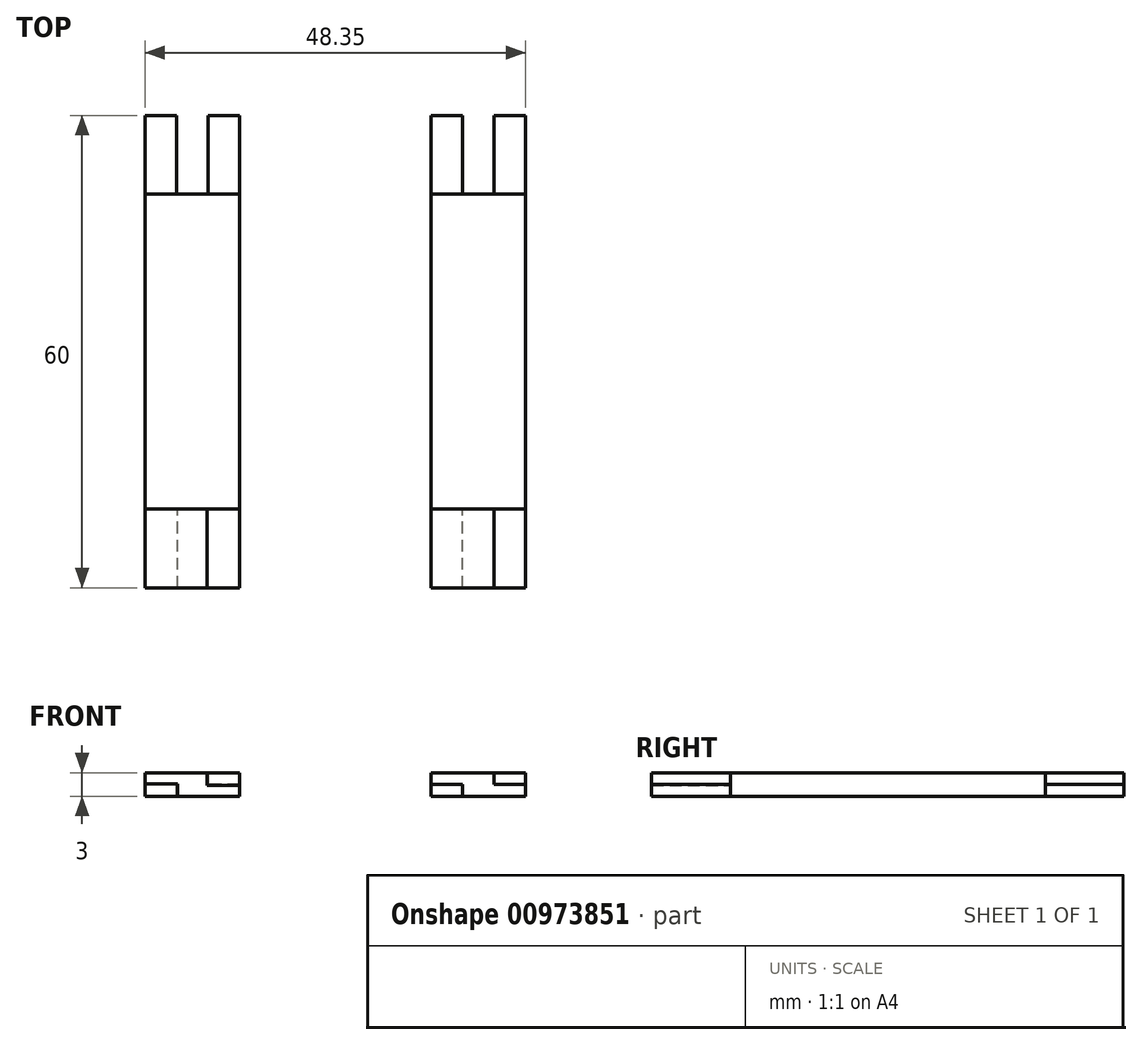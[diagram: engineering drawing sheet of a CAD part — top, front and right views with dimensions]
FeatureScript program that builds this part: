
annotation { "Feature Type Name" : "Feature", "Feature Type Description" : "" }
export const myFeature = defineFeature(function(context is Context, id is Id, definition is map)
    precondition{}
    {
        {
            var Q0;
            Q0=qCreatedBy(makeId("Top.planeOp"),FACE);
            var sketch = newSketch(context, id + "F0", { "sketchPlane" : qUnion([Q0])});
            skLineSegment(sketch, "E0.bottom", {"start": v(-16.75, 40) * mm, "end": v(-28.75, 40) * mm});
            skLineSegment(sketch, "E0.top", {"start": v(-16.75, 0) * mm, "end": v(-28.75, 0) * mm});
            skLineSegment(sketch, "E0.left", {"start": v(-16.75, 40) * mm, "end": v(-16.75, 0) * mm});
            skLineSegment(sketch, "E0.right", {"start": v(-28.75, 40) * mm, "end": v(-28.75, 0) * mm});
            skLineSegment(sketch, "E1.bottom", {"start": v(19.6, 40) * mm, "end": v(7.6, 40) * mm});
            skLineSegment(sketch, "E1.top", {"start": v(19.6, 0) * mm, "end": v(7.6, 0) * mm});
            skLineSegment(sketch, "E1.left", {"start": v(19.6, 40) * mm, "end": v(19.6, 0) * mm});
            skLineSegment(sketch, "E1.right", {"start": v(7.6, 40) * mm, "end": v(7.6, 0) * mm});
            skSolve(sketch);
        }
        {
            var Q0;
            Q0=makeQuery(id+"F0.imprint","IMPRINT",FACE,{"disambiguationData":[TD([[makeQuery(id+"F0.imprint","IMPRINT",EDGE,{"derivedFrom":sQuery(id+"F0.wireOp",EDGE,"E0.bottom")}),1.0]])]});
            var Q1;
            Q1=makeQuery(id+"F0.imprint","IMPRINT",FACE,{"disambiguationData":[TD([[makeQuery(id+"F0.imprint","IMPRINT",EDGE,{"derivedFrom":sQuery(id+"F0.wireOp",EDGE,"E1.bottom")}),1.0]])]});
            extrude(context, id + "F1", {"entities" : qUnion([Q0, Q1]), "depth" : 3 * mm, "offsetDistance" : 25 * mm});
        }
        {
            var Q0;
            Q0=makeQuery(id+"F1.opExtrude","SWEPT_FACE",FACE,{"disambiguationData":[OSD([sQuery(id+"F0.wireOp",EDGE,"E0.top")])]});
            var sketch = newSketch(context, id + "F2", { "sketchPlane" : qUnion([Q0])});
            skLineSegment(sketch, "E2", {"start": v(-28.75, 3) * mm, "end": v(-20.85, 3) * mm});
            skLineSegment(sketch, "E3", {"start": v(-20.85, 3) * mm, "end": v(-20.85, 1.4) * mm});
            skLineSegment(sketch, "E4", {"start": v(-20.85, 1.4) * mm, "end": v(-16.75, 1.4) * mm});
            skLineSegment(sketch, "E5", {"start": v(-16.75, 1.4) * mm, "end": v(-16.75, 0) * mm});
            skLineSegment(sketch, "E6", {"start": v(-16.75, 0) * mm, "end": v(-24.65, 0) * mm});
            skLineSegment(sketch, "E7", {"start": v(-24.65, 0) * mm, "end": v(-24.65, 1.6) * mm});
            skLineSegment(sketch, "E8", {"start": v(-24.65, 1.6) * mm, "end": v(-28.75, 1.6) * mm});
            skLineSegment(sketch, "E9", {"start": v(-28.75, 1.6) * mm, "end": v(-28.75, 3) * mm});
            skSolve(sketch);
        }
        {
            var Q0;
            Q0=makeQuery(id+"F1.opExtrude","SWEPT_FACE",FACE,{"disambiguationData":[OSD([sQuery(id+"F0.wireOp",EDGE,"E1.top")])]});
            var sketch = newSketch(context, id + "F3", { "sketchPlane" : qUnion([Q0])});
            skLineSegment(sketch, "E10", {"start": v(7.6, 3) * mm, "end": v(15.6, 3) * mm});
            skLineSegment(sketch, "E11", {"start": v(15.6, 3) * mm, "end": v(15.6, 1.5) * mm});
            skLineSegment(sketch, "E12", {"start": v(15.6, 1.5) * mm, "end": v(19.6, 1.5) * mm});
            skLineSegment(sketch, "E13", {"start": v(19.6, 1.5) * mm, "end": v(19.6, 0) * mm});
            skLineSegment(sketch, "E14", {"start": v(19.6, 0) * mm, "end": v(11.6, 0) * mm});
            skLineSegment(sketch, "E15", {"start": v(11.6, 0) * mm, "end": v(11.6, 1.5) * mm});
            skLineSegment(sketch, "E16", {"start": v(11.6, 1.5) * mm, "end": v(7.6, 1.5) * mm});
            skLineSegment(sketch, "E17", {"start": v(7.6, 1.5) * mm, "end": v(7.6, 3) * mm});
            skSolve(sketch);
        }
        {
            var Q0;
            Q0=makeQuery(id+"F2.imprint","IMPRINT",FACE,{"disambiguationData":[TD([[makeQuery(id+"F2.imprint","IMPRINT",EDGE,{"derivedFrom":sQuery(id+"F2.wireOp",EDGE,"5EJuN7WN-PZEX-N2uI-UbYe-ZOfutWstvHtY")}),1.0]])]});
            var Q1;
            Q1=makeQuery(id+"F3.imprint","IMPRINT",FACE,{"disambiguationData":[TD([[makeQuery(id+"F3.imprint","IMPRINT",EDGE,{"derivedFrom":sQuery(id+"F3.wireOp",EDGE,"E10")}),1.0]])]});
            var Q2;
            Q2=makeQuery(id+"F2.imprint","IMPRINT",FACE,{"disambiguationData":[TD([[makeQuery(id+"F2.imprint","IMPRINT",EDGE,{"derivedFrom":sQuery(id+"F2.wireOp",EDGE,"E2")}),1.0]])]});
            extrude(context, id + "F4", {"entities" : qUnion([Q0, Q1, Q2]), "depth" : 10 * mm, "offsetDistance" : 25 * mm});
        }
        {
            var Q0;
            Q0=makeQuery(id+"F1.opExtrude","SWEPT_FACE",FACE,{"disambiguationData":[OSD([sQuery(id+"F0.wireOp",EDGE,"E1.bottom")])]});
            var sketch = newSketch(context, id + "F5", { "sketchPlane" : qUnion([Q0])});
            skLineSegment(sketch, "E18", {"start": v(-19.6, 3) * mm, "end": v(-15.6, 3) * mm});
            skLineSegment(sketch, "E19", {"start": v(-15.6, 3) * mm, "end": v(-15.6, 1.5) * mm});
            skLineSegment(sketch, "E20", {"start": v(-15.6, 1.5) * mm, "end": v(-19.6, 1.5) * mm});
            skLineSegment(sketch, "E21", {"start": v(-19.6, 1.5) * mm, "end": v(-19.6, 3) * mm});
            skLineSegment(sketch, "E22.bottom", {"start": v(-7.6, 0) * mm, "end": v(-11.6, 0) * mm});
            skLineSegment(sketch, "E22.top", {"start": v(-7.6, 1.5) * mm, "end": v(-11.6, 1.5) * mm});
            skLineSegment(sketch, "E22.left", {"start": v(-7.6, 0) * mm, "end": v(-7.6, 1.5) * mm});
            skLineSegment(sketch, "E22.right", {"start": v(-11.6, 0) * mm, "end": v(-11.6, 1.5) * mm});
            skSolve(sketch);
        }
        {
            var Q0;
            Q0=makeQuery(id+"F1.opExtrude","SWEPT_FACE",FACE,{"disambiguationData":[OSD([sQuery(id+"F0.wireOp",EDGE,"E0.bottom")])]});
            var sketch = newSketch(context, id + "F6", { "sketchPlane" : qUnion([Q0])});
            skLineSegment(sketch, "E23.bottom", {"start": v(16.75, 3) * mm, "end": v(20.75, 3) * mm});
            skLineSegment(sketch, "E23.top", {"start": v(16.75, 1.5) * mm, "end": v(20.75, 1.5) * mm});
            skLineSegment(sketch, "E23.left", {"start": v(16.75, 3) * mm, "end": v(16.75, 1.5) * mm});
            skLineSegment(sketch, "E23.right", {"start": v(20.75, 3) * mm, "end": v(20.75, 1.5) * mm});
            skLineSegment(sketch, "E24.bottom", {"start": v(28.75, 0) * mm, "end": v(24.75, 0) * mm});
            skLineSegment(sketch, "E24.top", {"start": v(28.75, 1.5) * mm, "end": v(24.75, 1.5) * mm});
            skLineSegment(sketch, "E24.left", {"start": v(28.75, 0) * mm, "end": v(28.75, 1.5) * mm});
            skLineSegment(sketch, "E24.right", {"start": v(24.75, 0) * mm, "end": v(24.75, 1.5) * mm});
            skSolve(sketch);
        }
        {
            var Q0;
            Q0 = qSketchRegion(id + "F6", true);
            var Q1;
            Q1 = qSketchRegion(id + "F5", true);
            extrude(context, id + "F7", {"entities" : qUnion([Q0, Q1]), "depth" : 10 * mm, "offsetDistance" : 25 * mm});
        }
    });
